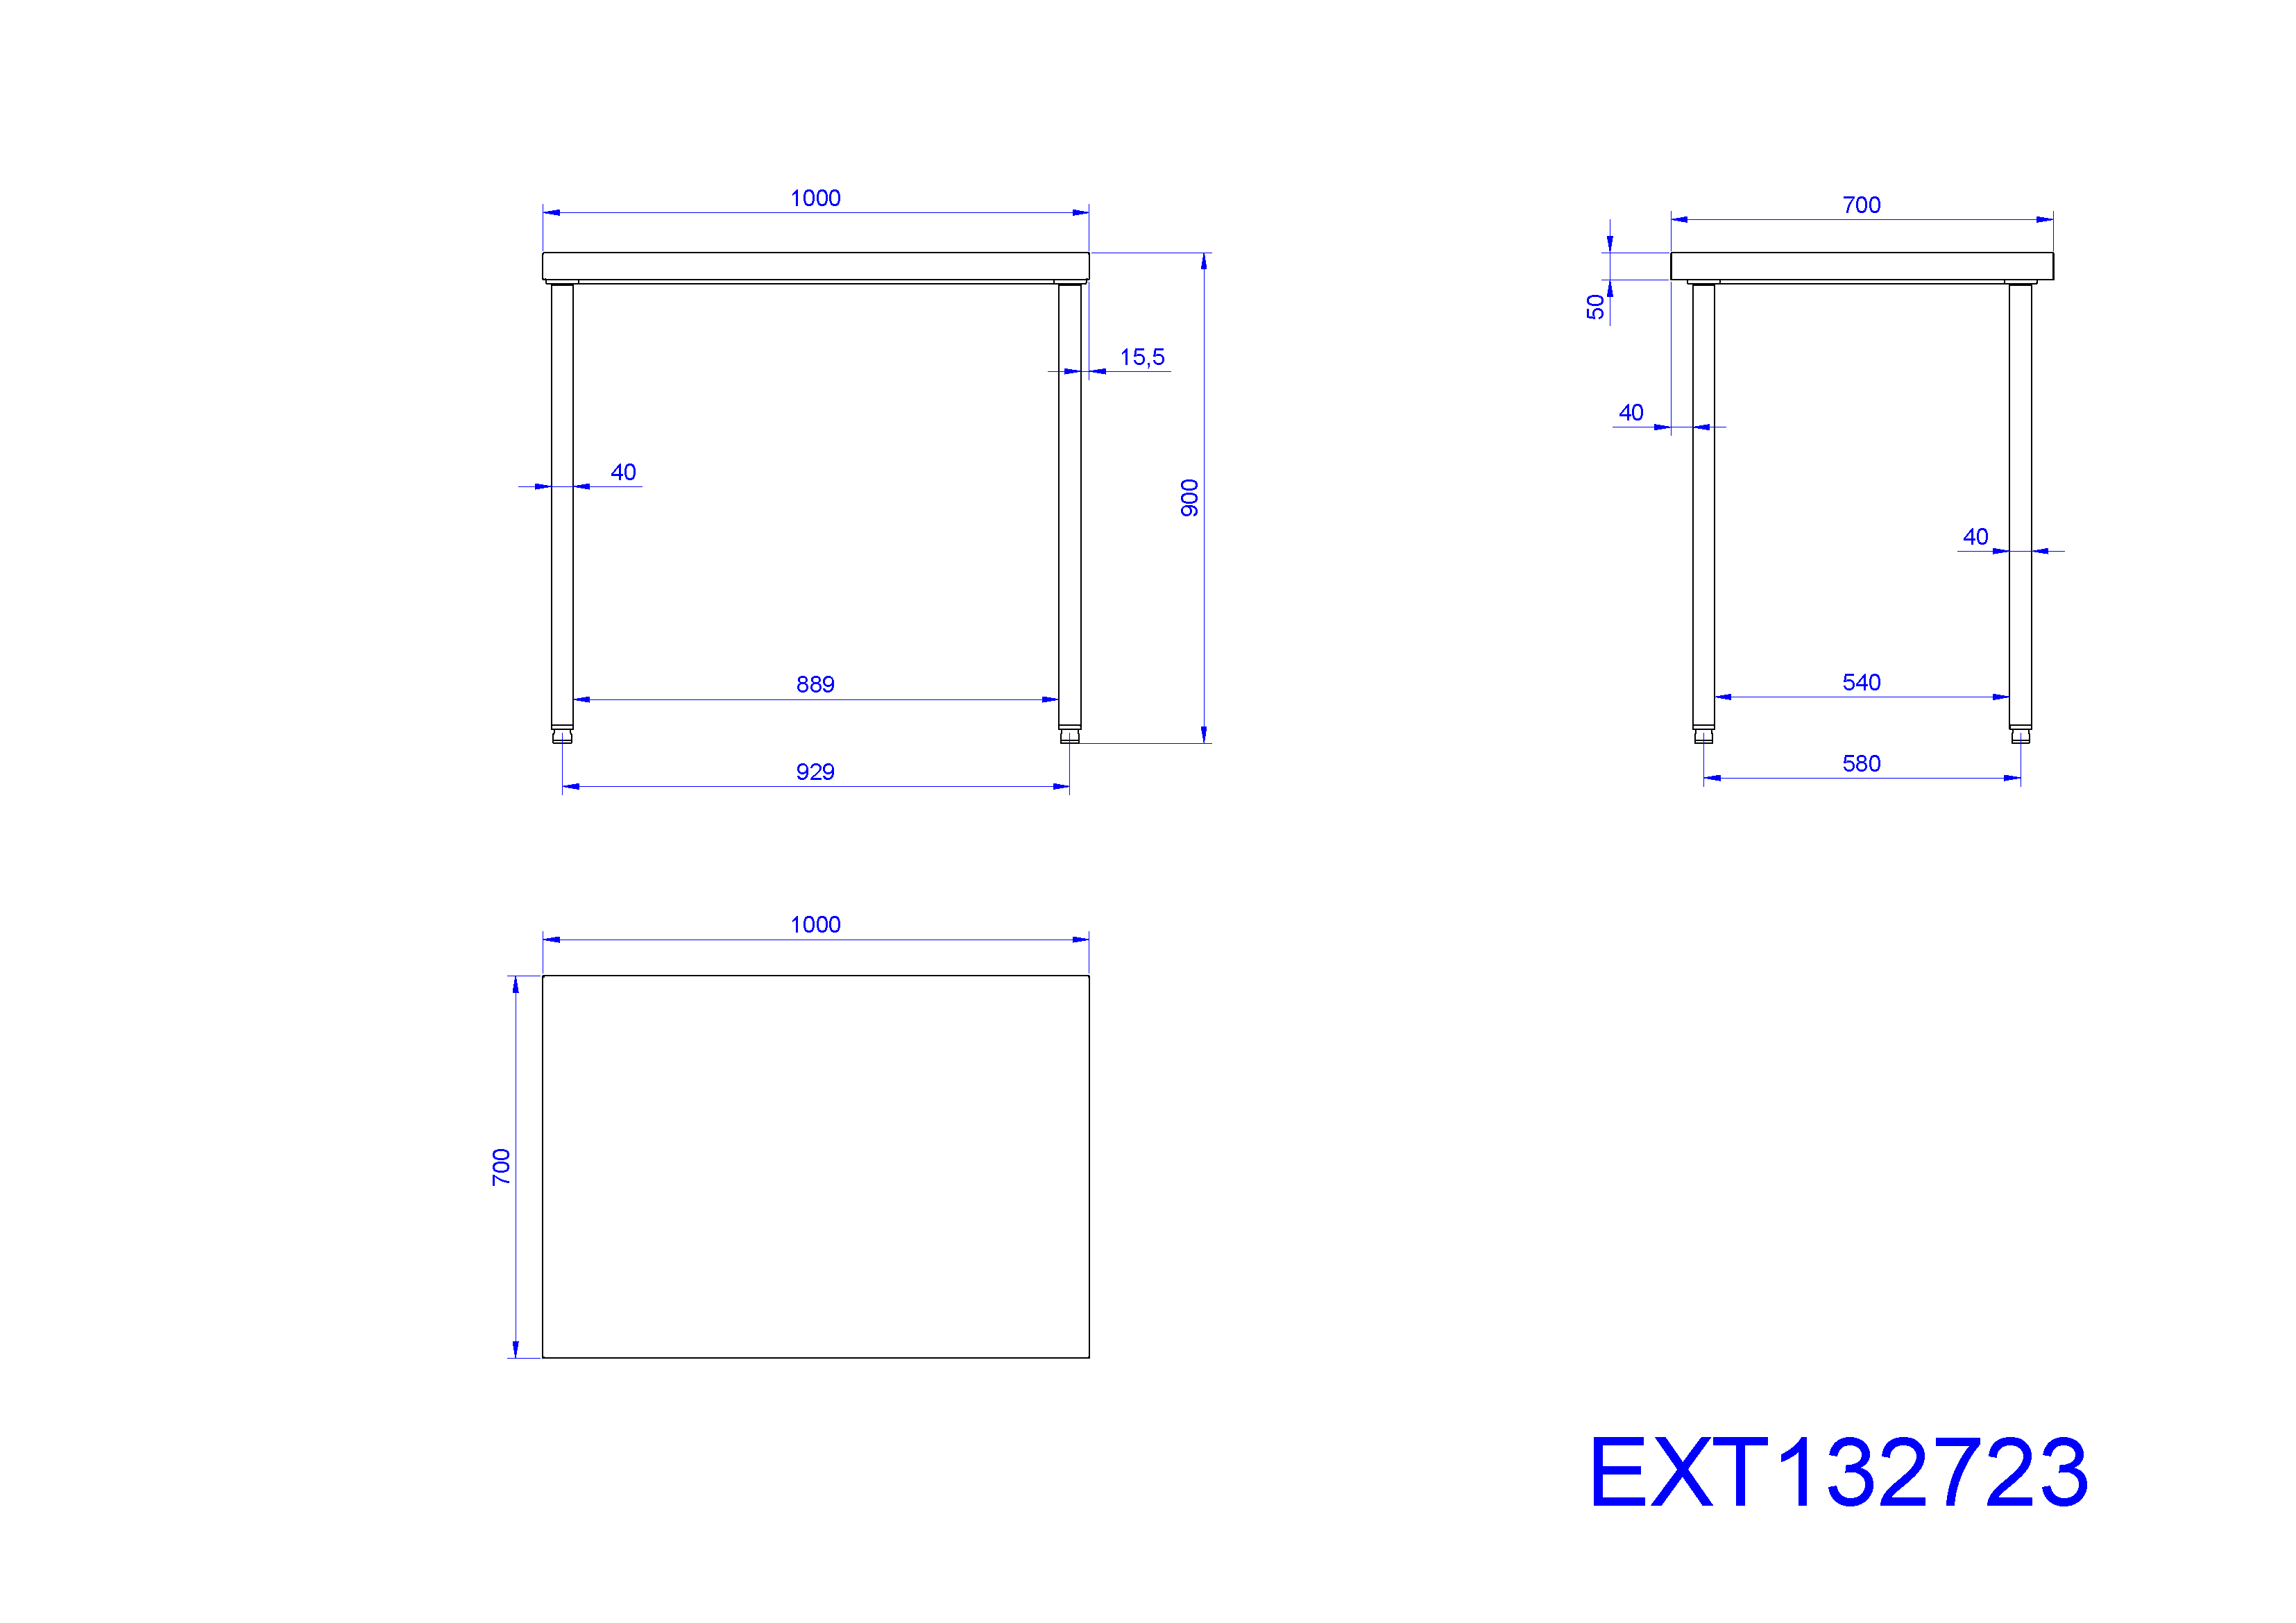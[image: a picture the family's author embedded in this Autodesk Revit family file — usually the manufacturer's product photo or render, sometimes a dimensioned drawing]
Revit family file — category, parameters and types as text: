
# Revit family: QF_ZANUSSI_132724_TG1200PN
name_source: partatom
category: Attrezzature speciali
units: mm (PartAtom-declared; Revit-internal decimal feet)

## family parameters
Basato su piano di lavoro = No
Condiviso = No
Punto di calcolo locali = No
Quota connettore circolare = Usa diametro
Sempre verticale = Sì
Taglio con vuoti quando caricato = No
Tipo di parte = Normale

## types (1)
- Standard
    Accessory = Sì
    Cold Water Size = 0 mm
    Compressed Air Pressure = 0.0 Pa
    Compressed Air Size = 0 mm
    Compressed Air Volume = 0.0 L/s
    Condensate Return Size = 0 mm
    Cycle = 0 Hz
    Depth Actual = 700 mm  [stored 2.29659 ft]
    Descrizione = WORK TABLE 1200 MM
    Direct Waste Size = 0 mm
    Gas Input Pressure = 0
    Gas KW = 0
    Gas Size = 0 mm
    HP = 0 HP
    Height Actual = 900 mm  [stored 2.95276 ft]
    Hot Water Size = 0 mm
    Item Number = 132724
    Length Actual = 1200 mm
    Modello = TG1200PN
    Phase = 0
    Produttore = Zanussi
    Prospetto di default = 0 mm  [stored 0 ft]
    Refrigerant Compressor Remote = Sì
    Refrigeration Liquid Line Size = 0 mm  [stored 0 ft]
    Refrigeration Suction Line Size = 0 mm  [stored 0 ft]
    Steam Consumption per Hour = 0
    Steam Supply Maximum Pressure = 0.0 Pa
    Steam Supply Minimum Pressure = 0.0 Pa
    Steam Supply Size = 0 mm
    URL = http://www.zanussiprofessional.com
    URL Manufacturer = http://www.zanussiprofessional.com
    Volts = 0 V
    Watts = 0 W
    Weight = 40.00 kg

note: source unit labels omitted for Gas Input Pressure — the stored unit's dimension contradicts the parameter name (converter mislabeling)

note: [stored X ft] marks values corroborated as IEEE doubles in the binary element streams (Revit-internal decimal feet)

## geometry (parser evidence)
native form markers: Sweep x2
no freeform markers — native parametric forms only
